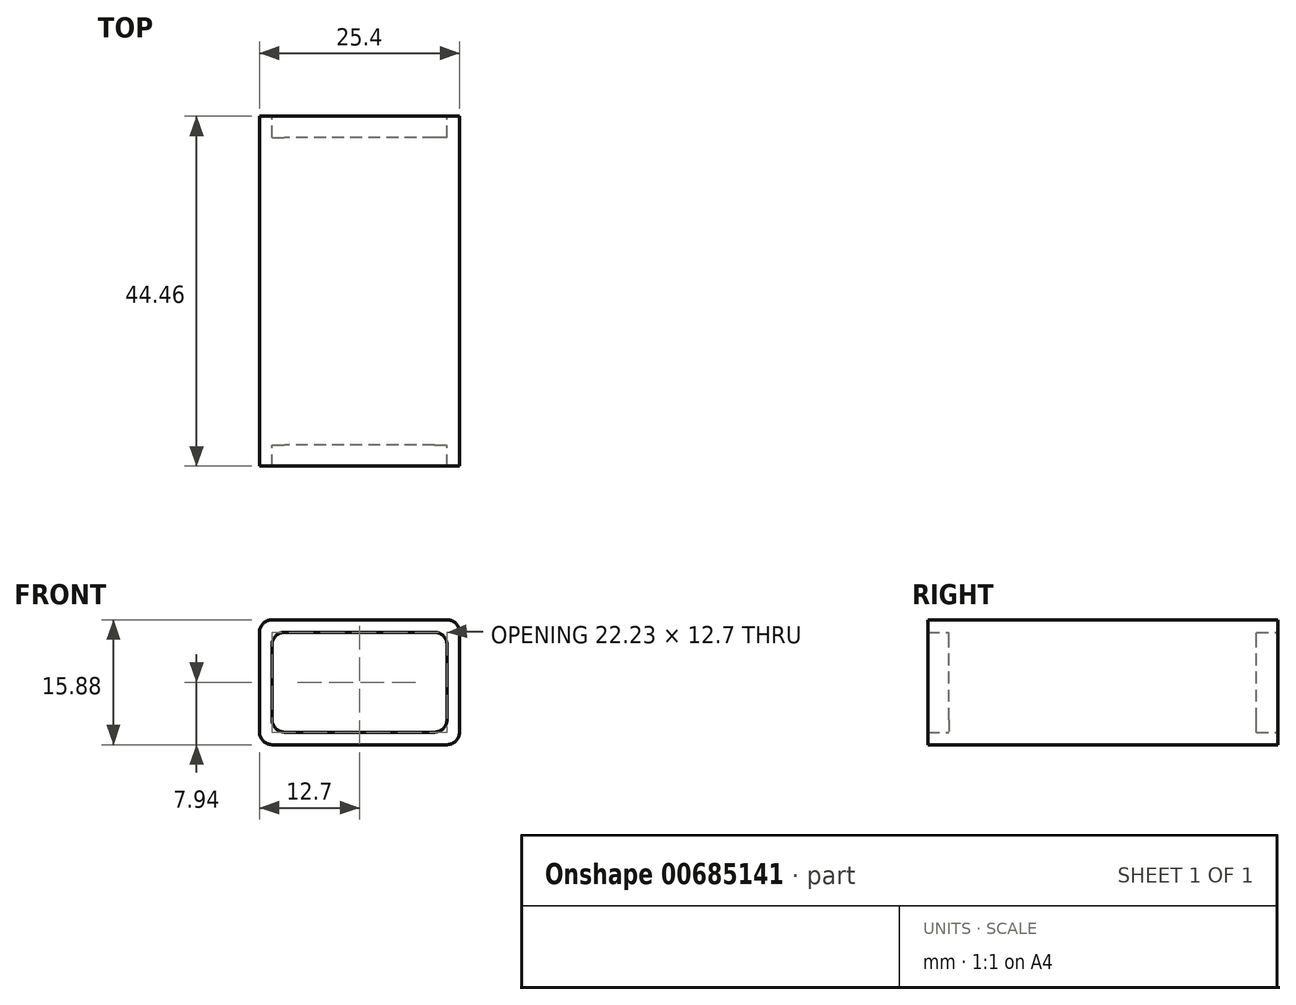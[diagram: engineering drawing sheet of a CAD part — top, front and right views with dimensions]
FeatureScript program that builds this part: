
annotation { "Feature Type Name" : "Feature", "Feature Type Description" : "" }
export const myFeature = defineFeature(function(context is Context, id is Id, definition is map)
    precondition{}
    {
        {
            var Q0;
            Q0=qCreatedBy(makeId("Front.planeOp"),FACE);
            var sketch = newSketch(context, id + "F0", { "sketchPlane" : qUnion([Q0])});
            skLineSegment(sketch, "E0.bottom", {"start": v(12.7, -7.94) * mm, "end": v(-12.7, -7.94) * mm});
            skLineSegment(sketch, "E0.top", {"start": v(12.7, 7.94) * mm, "end": v(-12.7, 7.94) * mm});
            skLineSegment(sketch, "E0.left", {"start": v(12.7, -7.94) * mm, "end": v(12.7, 7.94) * mm});
            skLineSegment(sketch, "E0.right", {"start": v(-12.7, -7.94) * mm, "end": v(-12.7, 7.94) * mm});
            skPoint(sketch, "E0.middle", {"position": v(0, 0) * mm});
            skSolve(sketch);
        }
        {
            var Q0;
            Q0=makeQuery(id+"F0.imprint","IMPRINT",FACE,{"disambiguationData":[TD([[makeQuery(id+"F0.imprint","IMPRINT",EDGE,{"derivedFrom":sQuery(id+"F0.wireOp",EDGE,"E0.bottom")}),-1.0]])]});
            extrude(context, id + "F1", {"entities" : qUnion([Q0]), "endBound" : BoundingType.SYMMETRIC, "depth" : 44.45 * mm, "offsetDistance" : 25.4 * mm});
        }
        {
            var Q0;
            Q0=makeQuery(id+"F1.opExtrude","CAP_FACE",FACE,{"disambiguationData":[OSD([sQuery(id+"F0.wireOp",EDGE,"E0.bottom"),sQuery(id+"F0.wireOp",EDGE,"E0.top"),sQuery(id+"F0.wireOp",EDGE,"E0.left"),sQuery(id+"F0.wireOp",EDGE,"E0.right")])],"isStart":false});
            var Q1;
            Q1=makeQuery(id+"F1.opExtrude","CAP_FACE",FACE,{"disambiguationData":[OSD([sQuery(id+"F0.wireOp",EDGE,"E0.bottom"),sQuery(id+"F0.wireOp",EDGE,"E0.top"),sQuery(id+"F0.wireOp",EDGE,"E0.left"),sQuery(id+"F0.wireOp",EDGE,"E0.right")])],"isStart":true});
            shell(context, id + "F2", {"entities" : qUnion([Q0, Q1]), "thickness" : 1.59 * mm});
        }
        {
            var Q0;
            Q0=qCreatedBy(makeId("Front.planeOp"),FACE);
            var sketch = newSketch(context, id + "F3", { "sketchPlane" : qUnion([Q0])});
            skLineSegment(sketch, "E1.bottom", {"start": v(11.9, -7.14) * mm, "end": v(-11.9, -7.14) * mm});
            skLineSegment(sketch, "E1.top", {"start": v(11.9, 7.14) * mm, "end": v(-11.9, 7.14) * mm});
            skLineSegment(sketch, "E1.left", {"start": v(11.9, -7.14) * mm, "end": v(11.9, 7.14) * mm});
            skLineSegment(sketch, "E1.right", {"start": v(-11.9, -7.14) * mm, "end": v(-11.9, 7.14) * mm});
            skPoint(sketch, "E1.middle", {"position": v(0, 0) * mm});
            skSolve(sketch);
        }
        {
            var Q0;
            Q0 = qSketchRegion(id + "F3", true);
            extrude(context, id + "F4", {"entities" : qUnion([Q0]), "operationType" : NewBodyOperationType.ADD, "endBound" : BoundingType.SYMMETRIC, "depth" : 39.07 * mm, "offsetDistance" : 25.4 * mm});
        }
        {
            var Q0;
            {var subQ0=sQuery(id+"F0.wireOp",EDGE,"E0.right");var subQ1=sQuery(id+"F0.wireOp",EDGE,"E0.top");Q0=makeQuery(id+"F4.boolean.opBoolean","SPLIT",EDGE,{"disambiguationData":[TD([makeQuery(id+"F1.opExtrude","CAP_FACE",FACE,{"disambiguationData":[OSD([sQuery(id+"F0.wireOp",EDGE,"E0.bottom"),subQ1,sQuery(id+"F0.wireOp",EDGE,"E0.left"),subQ0])],"isStart":false})])],"derivedFrom":makeQuery(id+"F2.opShell","OFFSET_EDGE",EDGE,{"disambiguationData":[OSD([subQ1,subQ0])]})});}
            var Q1;
            {var subQ0=sQuery(id+"F0.wireOp",EDGE,"E0.left");var subQ1=sQuery(id+"F0.wireOp",EDGE,"E0.top");Q1=makeQuery(id+"F4.boolean.opBoolean","SPLIT",EDGE,{"disambiguationData":[TD([makeQuery(id+"F1.opExtrude","CAP_FACE",FACE,{"disambiguationData":[OSD([sQuery(id+"F0.wireOp",EDGE,"E0.bottom"),subQ1,subQ0,sQuery(id+"F0.wireOp",EDGE,"E0.right")])],"isStart":false})])],"derivedFrom":makeQuery(id+"F2.opShell","OFFSET_EDGE",EDGE,{"disambiguationData":[OSD([subQ1,subQ0])]})});}
            var Q2;
            {var subQ0=sQuery(id+"F0.wireOp",EDGE,"E0.left");var subQ1=sQuery(id+"F0.wireOp",EDGE,"E0.bottom");Q2=makeQuery(id+"F4.boolean.opBoolean","SPLIT",EDGE,{"disambiguationData":[TD([makeQuery(id+"F1.opExtrude","CAP_FACE",FACE,{"disambiguationData":[OSD([subQ1,sQuery(id+"F0.wireOp",EDGE,"E0.top"),subQ0,sQuery(id+"F0.wireOp",EDGE,"E0.right")])],"isStart":false})])],"derivedFrom":makeQuery(id+"F2.opShell","OFFSET_EDGE",EDGE,{"disambiguationData":[OSD([subQ1,subQ0])]})});}
            var Q3;
            {var subQ0=sQuery(id+"F0.wireOp",EDGE,"E0.right");var subQ1=sQuery(id+"F0.wireOp",EDGE,"E0.bottom");Q3=makeQuery(id+"F4.boolean.opBoolean","SPLIT",EDGE,{"disambiguationData":[TD([makeQuery(id+"F1.opExtrude","CAP_FACE",FACE,{"disambiguationData":[OSD([subQ1,sQuery(id+"F0.wireOp",EDGE,"E0.top"),sQuery(id+"F0.wireOp",EDGE,"E0.left"),subQ0])],"isStart":false})])],"derivedFrom":makeQuery(id+"F2.opShell","OFFSET_EDGE",EDGE,{"disambiguationData":[OSD([subQ1,subQ0])]})});}
            var Q4;
            {var subQ0=sQuery(id+"F0.wireOp",EDGE,"E0.right");var subQ1=sQuery(id+"F0.wireOp",EDGE,"E0.bottom");Q4=makeQuery(id+"F4.boolean.opBoolean","SPLIT",EDGE,{"disambiguationData":[TD([makeQuery(id+"F1.opExtrude","CAP_FACE",FACE,{"disambiguationData":[OSD([subQ1,sQuery(id+"F0.wireOp",EDGE,"E0.top"),sQuery(id+"F0.wireOp",EDGE,"E0.left"),subQ0])],"isStart":true})])],"derivedFrom":makeQuery(id+"F2.opShell","OFFSET_EDGE",EDGE,{"disambiguationData":[OSD([subQ1,subQ0])]})});}
            var Q5;
            {var subQ0=sQuery(id+"F0.wireOp",EDGE,"E0.left");var subQ1=sQuery(id+"F0.wireOp",EDGE,"E0.bottom");Q5=makeQuery(id+"F4.boolean.opBoolean","SPLIT",EDGE,{"disambiguationData":[TD([makeQuery(id+"F1.opExtrude","CAP_FACE",FACE,{"disambiguationData":[OSD([subQ1,sQuery(id+"F0.wireOp",EDGE,"E0.top"),subQ0,sQuery(id+"F0.wireOp",EDGE,"E0.right")])],"isStart":true})])],"derivedFrom":makeQuery(id+"F2.opShell","OFFSET_EDGE",EDGE,{"disambiguationData":[OSD([subQ1,subQ0])]})});}
            var Q6;
            {var subQ0=sQuery(id+"F0.wireOp",EDGE,"E0.right");var subQ1=sQuery(id+"F0.wireOp",EDGE,"E0.top");Q6=makeQuery(id+"F4.boolean.opBoolean","SPLIT",EDGE,{"disambiguationData":[TD([makeQuery(id+"F1.opExtrude","CAP_FACE",FACE,{"disambiguationData":[OSD([sQuery(id+"F0.wireOp",EDGE,"E0.bottom"),subQ1,sQuery(id+"F0.wireOp",EDGE,"E0.left"),subQ0])],"isStart":true})])],"derivedFrom":makeQuery(id+"F2.opShell","OFFSET_EDGE",EDGE,{"disambiguationData":[OSD([subQ1,subQ0])]})});}
            var Q7;
            {var subQ0=sQuery(id+"F0.wireOp",EDGE,"E0.left");var subQ1=sQuery(id+"F0.wireOp",EDGE,"E0.top");Q7=makeQuery(id+"F4.boolean.opBoolean","SPLIT",EDGE,{"disambiguationData":[TD([makeQuery(id+"F1.opExtrude","CAP_FACE",FACE,{"disambiguationData":[OSD([sQuery(id+"F0.wireOp",EDGE,"E0.bottom"),subQ1,subQ0,sQuery(id+"F0.wireOp",EDGE,"E0.right")])],"isStart":true})])],"derivedFrom":makeQuery(id+"F2.opShell","OFFSET_EDGE",EDGE,{"disambiguationData":[OSD([subQ1,subQ0])]})});}
            fillet(context, id + "F5", {"entities" : qUnion([Q0, Q1, Q2, Q3, Q4, Q5, Q6, Q7]), "radius" : 1.59 * mm, "tangentPropagation" : true, "allowEdgeOverflow" : false});
        }
        {
            var Q0;
            Q0=makeQuery(id+"F1.opExtrude","SWEPT_EDGE",EDGE,{"disambiguationData":[OSD([sQuery(id+"F0.wireOp",EDGE,"E0.bottom"),sQuery(id+"F0.wireOp",EDGE,"E0.right")])]});
            var Q1;
            Q1=makeQuery(id+"F1.opExtrude","SWEPT_EDGE",EDGE,{"disambiguationData":[OSD([sQuery(id+"F0.wireOp",EDGE,"E0.top"),sQuery(id+"F0.wireOp",EDGE,"E0.right")])]});
            var Q2;
            Q2=makeQuery(id+"F1.opExtrude","SWEPT_EDGE",EDGE,{"disambiguationData":[OSD([sQuery(id+"F0.wireOp",EDGE,"E0.top"),sQuery(id+"F0.wireOp",EDGE,"E0.left")])]});
            var Q3;
            Q3=makeQuery(id+"F1.opExtrude","SWEPT_EDGE",EDGE,{"disambiguationData":[OSD([sQuery(id+"F0.wireOp",EDGE,"E0.bottom"),sQuery(id+"F0.wireOp",EDGE,"E0.left")])]});
            fillet(context, id + "F6", {"entities" : qUnion([Q0, Q1, Q2, Q3]), "radius" : 1.59 * mm, "tangentPropagation" : true, "allowEdgeOverflow" : false});
        }
    });
